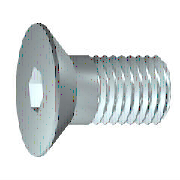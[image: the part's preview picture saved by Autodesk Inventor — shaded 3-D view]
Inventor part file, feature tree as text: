
AUTODESK INVENTOR PART (.ipt)
format: ipt  version: 2020 (Build 240168000, 168)  size: 185,344 bytes
history: native  units: mm (DEFAULTED — no unit token found)
features: other x4, sketch x3, fillet x1, chamfer x1
ambient origin geometry x8: Origin, YZ Plane, XZ Plane, XY Plane, X Axis, Y Axis, Z Axis, Center Point
bodies: Solid1 (feature_tree)
feature tree (9):
  sketch  "Sketch1"  dims[d2=3.0mm]
  other  "WorkPoint1"
  sketch  "Sketch2"  dims[d3=3.0mm]
  fillet  "Fillet1"  [1 undecoded]
  chamfer  "Chamfer1"  Distance=1.5mm
  other  "MSC_A1"
  other  "MSC_PF1"
  other  "MSC_PT1"
  sketch  "Sketch3"  dims[d4=1.5mm d5=1.5mm d6=8.0mm d7=25.0mm d8=360.0deg d9=0.0mm d10=2.0mm d11=2.0mm d12=120.0deg d13=120.0deg d14=120.0deg d15=120.0deg d16=1.2mm d17=0.0mm d18=0.1mm d19=0.25mm d20=45.0deg d22=0.0mm d23=0.0mm d35=0.0mm d37=0.0mm d38=0.0mm d39=0.25mm d40=0.0mm d41=0.0mm d42=0.0mm d43=45.0deg]
note: 1 required parameter value undecoded (feature->parameter linkage not recoverable at this tier; creation-order binding heuristic only, values carry confidence <= 0.55)
